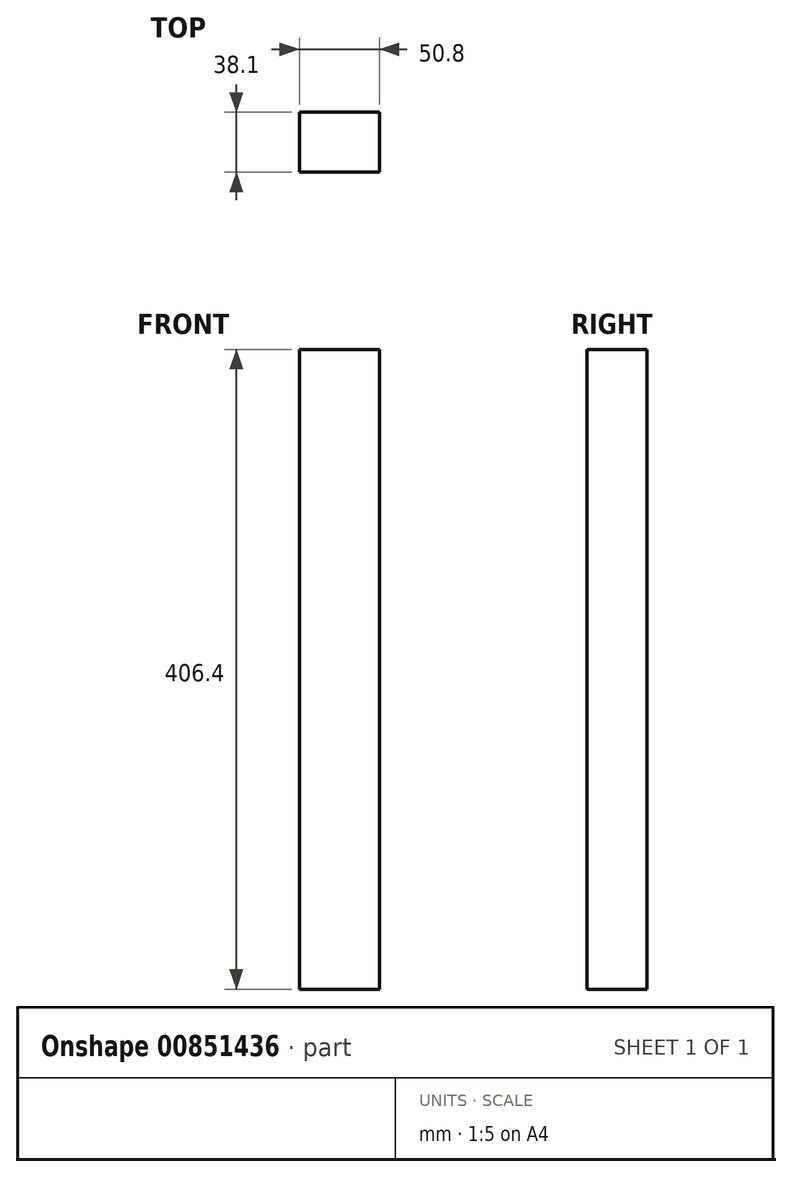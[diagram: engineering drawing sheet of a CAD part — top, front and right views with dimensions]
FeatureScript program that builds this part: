
annotation { "Feature Type Name" : "Feature", "Feature Type Description" : "" }
export const myFeature = defineFeature(function(context is Context, id is Id, definition is map)
    precondition{}
    {
        {
            var Q0;
            Q0=qCreatedBy(makeId("Front.planeOp"),FACE);
            var sketch = newSketch(context, id + "F0", { "sketchPlane" : qUnion([Q0])});
            skLineSegment(sketch, "E0.bottom", {"start": v(0, 0) * mm, "end": v(50.8, 0) * mm});
            skLineSegment(sketch, "E0.top", {"start": v(0, -406.4) * mm, "end": v(50.8, -406.4) * mm});
            skLineSegment(sketch, "E0.left", {"start": v(0, 0) * mm, "end": v(0, -406.4) * mm});
            skLineSegment(sketch, "E0.right", {"start": v(50.8, 0) * mm, "end": v(50.8, -406.4) * mm});
            skSolve(sketch);
        }
        {
            var Q0;
            Q0 = qSketchRegion(id + "F0", true);
            extrude(context, id + "F1", {"entities" : qUnion([Q0]), "depth" : 38.1 * mm, "offsetDistance" : 25.4 * mm});
        }
    });
